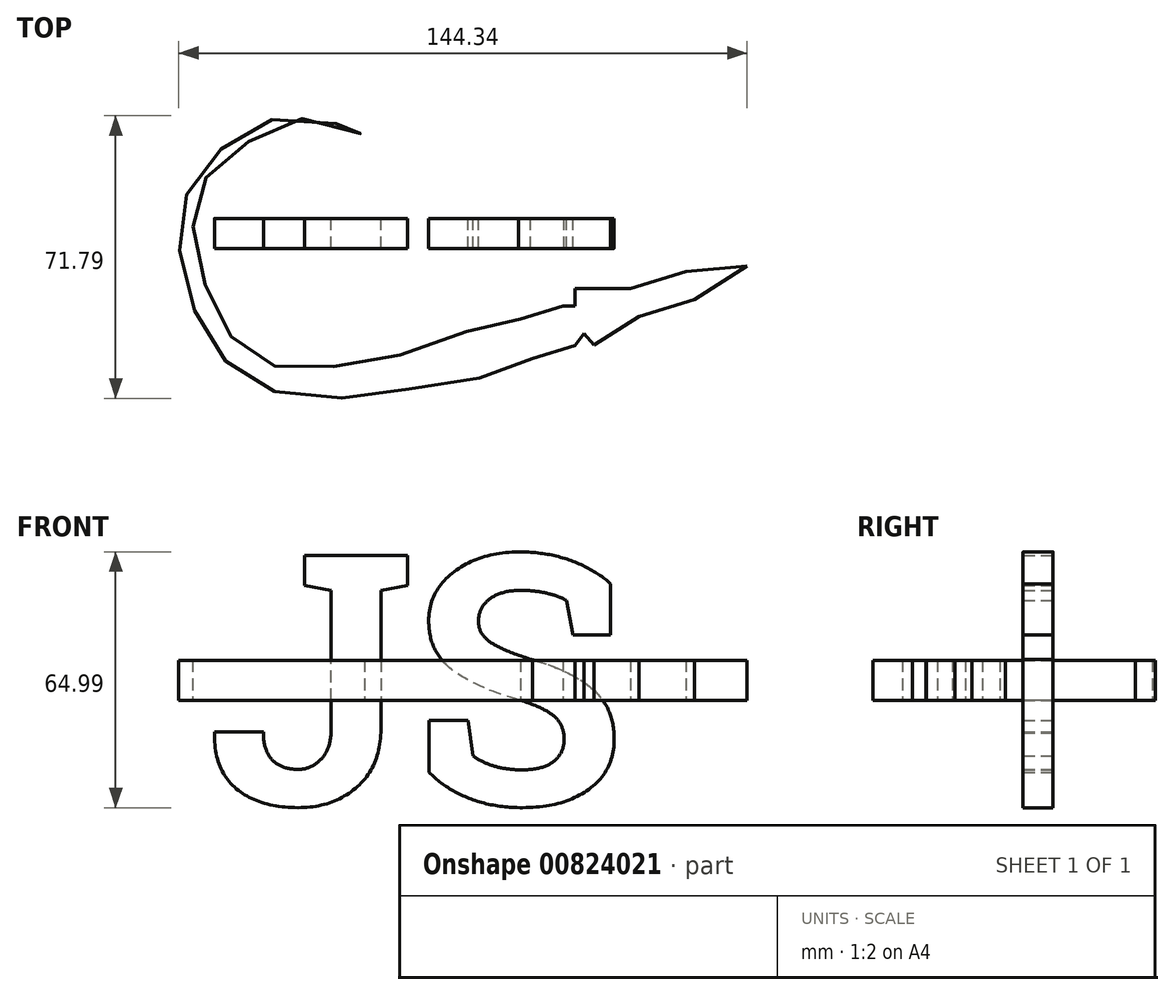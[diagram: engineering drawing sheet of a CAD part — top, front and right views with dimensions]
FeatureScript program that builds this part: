
annotation { "Feature Type Name" : "Feature", "Feature Type Description" : "" }
export const myFeature = defineFeature(function(context is Context, id is Id, definition is map)
    precondition{}
    {
        {
            var Q0;
            Q0=qCreatedBy(makeId("Front.planeOp"),FACE);
            var sketch = newSketch(context, id + "F0", { "sketchPlane" : qUnion([Q0])});
            skText(sketch, "E0", { "text": "JS", "fontName": "RobotoSlab-Bold.ttf"});
            const initialGuessF0  = {"E0": [-0.06776, -0.03143, 1, 0, 0.064]};
            skSetInitialGuess(sketch, initialGuessF0);
            skSolve(sketch);
        }
        {
            var Q0;
            Q0=makeQuery(id+"F0.imprint","IMPRINT",FACE,{"disambiguationData":[TD([[makeQuery(id+"F0.imprint","IMPRINT",EDGE,{"derivedFrom":sQuery(id+"F0.wireOp",EDGE,"E0.sketch_text.stroke-18")}),-1.0]])]});
            var Q1;
            Q1=makeQuery(id+"F0.imprint","IMPRINT",FACE,{"disambiguationData":[TD([[makeQuery(id+"F0.imprint","IMPRINT",EDGE,{"derivedFrom":sQuery(id+"F0.wireOp",EDGE,"E0.sketch_text.stroke-0")}),-1.0]])]});
            extrude(context, id + "F1", {"entities" : qUnion([Q0, Q1]), "depth" : 7.62 * mm, "offsetDistance" : 25.4 * mm});
        }
        {
            var Q0;
            Q0=qCreatedBy(makeId("Top.planeOp"),FACE);
            var sketch = newSketch(context, id + "F2", { "sketchPlane" : qUnion([Q0])});
            skFitSpline(sketch, "E1", {"points": [v(-28.05, 20.99) * mm, v(-41.5, 25.73) * mm, v(-60.56, 20.72) * mm, v(-72.83, 7.14) * mm, v(-74.9, -10.5) * mm, v(-67.72, -30.36) * mm, v(-54.9, -42.52) * mm, v(-30.71, -45.48) * mm, v(-4.82, -41.26) * mm, v(14.6, -35.63) * mm, v(11.49, -25.58) * mm, v(-6.98, -30.95) * mm, v(-32.37, -37.11) * mm, v(-52.21, -37.15) * mm, v(-63.93, -27.29) * mm, v(-70.73, -8.88) * mm, v(-70.32, 7.28) * mm, v(-58.98, 18.55) * mm, v(-41.37, 25.25) * mm, v(-28.05, 20.99) * mm]});
            skLineSegment(sketch, "E2", {"start": v(11.49, -25.58) * mm, "end": v(14.6, -35.63) * mm});
            skLineSegment(sketch, "E3", {"start": v(11.49, -25.58) * mm, "end": v(22.28, -22.24) * mm});
            skLineSegment(sketch, "E4", {"start": v(14.6, -35.63) * mm, "end": v(25.4, -32.3) * mm});
            skLineSegment(sketch, "E5", {"start": v(25.4, -32.3) * mm, "end": v(22.28, -22.24) * mm});
            skLineSegment(sketch, "E6", {"start": v(22.28, -22.24) * mm, "end": v(25.4, -22.24) * mm});
            skLineSegment(sketch, "E7", {"start": v(25.4, -22.24) * mm, "end": v(27.6, -29.3) * mm});
            skLineSegment(sketch, "E8", {"start": v(27.6, -29.3) * mm, "end": v(25.4, -32.3) * mm});
            skLineSegment(sketch, "E9", {"start": v(25.4, -22.24) * mm, "end": v(53.6, -13.49) * mm});
            skLineSegment(sketch, "E10", {"start": v(27.6, -29.3) * mm, "end": v(55.65, -20.6) * mm});
            skLineSegment(sketch, "E11", {"start": v(55.65, -20.6) * mm, "end": v(69.03, -12.09) * mm});
            skLineSegment(sketch, "E12", {"start": v(69.03, -12.09) * mm, "end": v(53.6, -13.49) * mm});
            skLineSegment(sketch, "E13", {"start": v(39.5, -17.86) * mm, "end": v(25.4, -17.86) * mm});
            skLineSegment(sketch, "E14", {"start": v(25.4, -17.86) * mm, "end": v(25.4, -22.24) * mm});
            skLineSegment(sketch, "E15", {"start": v(41.62, -24.94) * mm, "end": v(30.22, -32.13) * mm});
            skLineSegment(sketch, "E16", {"start": v(27.6, -29.3) * mm, "end": v(30.22, -32.13) * mm});
            skSolve(sketch);
        }
        {
            var Q0;
            Q0 = qSketchRegion(id + "F2", true);
            extrude(context, id + "F3", {"entities" : qUnion([Q0]), "depth" : 5.08 * mm, "offsetDistance" : 25.4 * mm, "hasSecondDirection" : true, "secondDirectionOppositeDirection" : true, "secondDirectionDepth" : 5.08 * mm});
        }
    });
